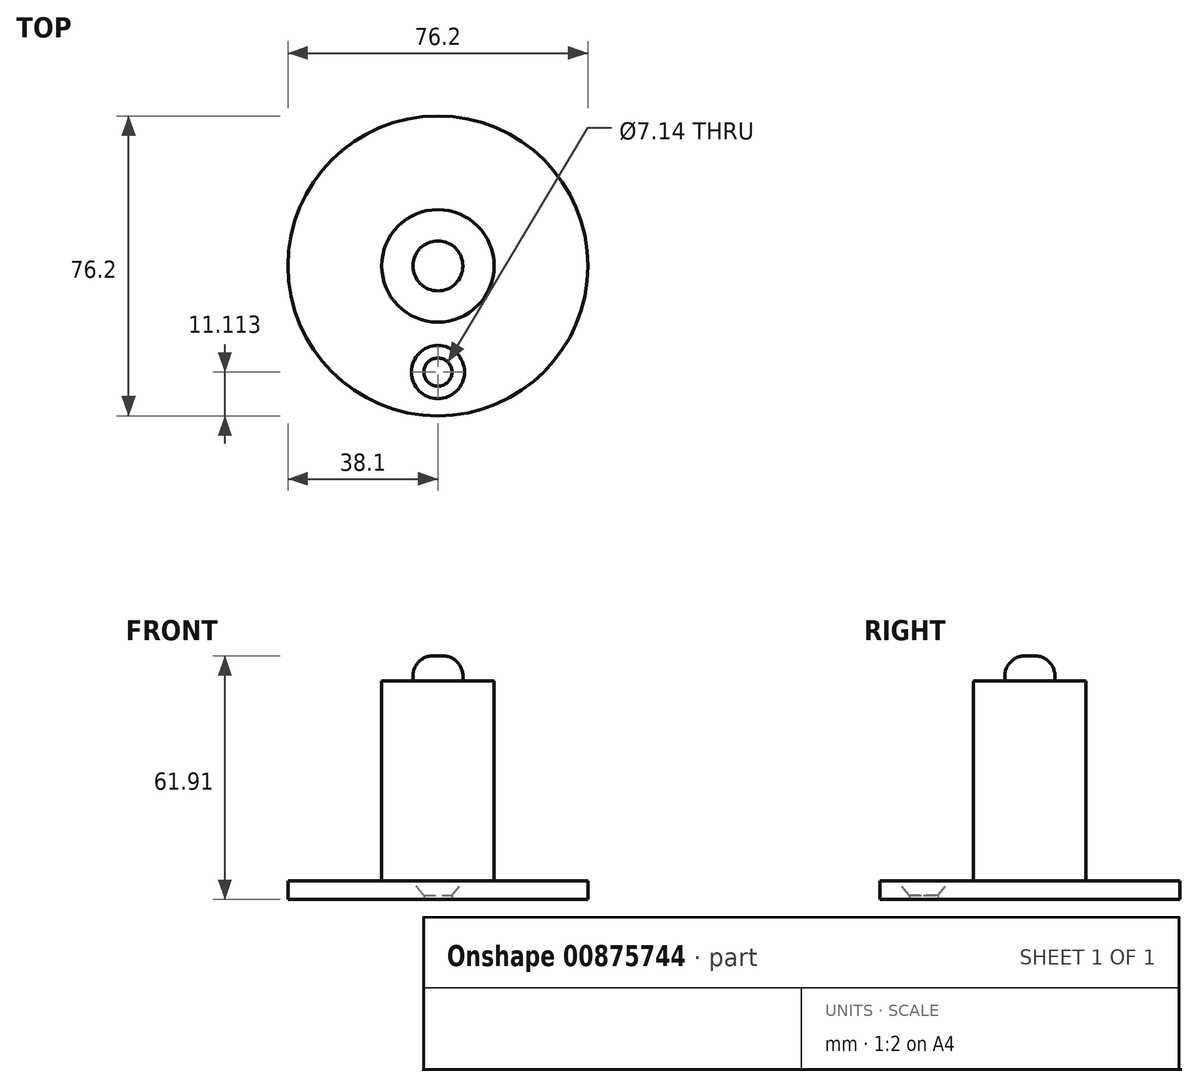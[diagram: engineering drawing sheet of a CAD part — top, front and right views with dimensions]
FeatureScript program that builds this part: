
annotation { "Feature Type Name" : "Feature", "Feature Type Description" : "" }
export const myFeature = defineFeature(function(context is Context, id is Id, definition is map)
    precondition{}
    {
        {
            var Q0;
            Q0=qCreatedBy(makeId("Top.planeOp"),FACE);
            var sketch = newSketch(context, id + "F0", { "sketchPlane" : qUnion([Q0])});
            skCircle(sketch, "E0", {"center": v(0, 0) * mm, "radius": 38.1 * mm});
            skSolve(sketch);
        }
        {
            var Q0;
            Q0=makeQuery(id+"F0.imprint","IMPRINT",FACE,{"disambiguationData":[TD([[makeQuery(id+"F0.imprint","IMPRINT",EDGE,{"derivedFrom":sQuery(id+"F0.wireOp",EDGE,"E0")}),1.0]])]});
            extrude(context, id + "F1", {"entities" : qUnion([Q0]), "depth" : 4.76 * mm, "offsetDistance" : 25.4 * mm});
        }
        {
            var Q0;
            Q0=makeQuery(id+"F1.opExtrude","CAP_FACE",FACE,{"disambiguationData":[OSD([sQuery(id+"F0.wireOp",EDGE,"E0")])],"isStart":false});
            var sketch = newSketch(context, id + "F2", { "sketchPlane" : qUnion([Q0])});
            skCircle(sketch, "E1", {"center": v(0, 0) * mm, "radius": 14.29 * mm});
            skSolve(sketch);
        }
        {
            var Q0;
            Q0=makeQuery(id+"F2.imprint","IMPRINT",FACE,{"disambiguationData":[TD([[makeQuery(id+"F2.imprint","IMPRINT",EDGE,{"derivedFrom":sQuery(id+"F2.wireOp",EDGE,"E1")}),1.0]])]});
            extrude(context, id + "F3", {"entities" : qUnion([Q0]), "operationType" : NewBodyOperationType.ADD, "depth" : 50.8 * mm, "offsetDistance" : 25.4 * mm});
        }
        {
            var Q0;
            Q0=makeQuery(id+"F3.opExtrude","CAP_FACE",FACE,{"disambiguationData":[OSD([sQuery(id+"F2.wireOp",EDGE,"E1")])],"isStart":false});
            var sketch = newSketch(context, id + "F4", { "sketchPlane" : qUnion([Q0])});
            skCircle(sketch, "E2", {"center": v(0, 0) * mm, "radius": 6.35 * mm});
            skSolve(sketch);
        }
        {
            var Q0;
            Q0=makeQuery(id+"F4.imprint","IMPRINT",FACE,{"disambiguationData":[TD([[makeQuery(id+"F4.imprint","IMPRINT",EDGE,{"derivedFrom":sQuery(id+"F4.wireOp",EDGE,"E2")}),1.0]])]});
            extrude(context, id + "F5", {"entities" : qUnion([Q0]), "operationType" : NewBodyOperationType.ADD, "depth" : 6.35 * mm, "offsetDistance" : 25.4 * mm});
        }
        {
            var Q0;
            Q0=makeQuery(id+"F5.opExtrude","CAP_EDGE",EDGE,{"disambiguationData":[OSD([sQuery(id+"F4.wireOp",EDGE,"E2")])],"isStart":false});
            fillet(context, id + "F6", {"entities" : qUnion([Q0]), "radius" : 5.08 * mm, "tangentPropagation" : true, "allowEdgeOverflow" : false});
        }
        {
            var Q0;
            Q0=makeQuery(id+"F1.opExtrude","CAP_FACE",FACE,{"disambiguationData":[OSD([sQuery(id+"F0.wireOp",EDGE,"E0")])],"isStart":false});
            var sketch = newSketch(context, id + "F7", { "sketchPlane" : qUnion([Q0])});
            skPoint(sketch, "E3", {"position": v(0, -26.99) * mm});
            skSolve(sketch);
        }
        {
            var Q0;
            Q0=sQuery(id+"F7.wireOp",VERTEX,"E3");
            var Q1;
            Q1=makeQuery(id+"F1.opExtrude","SWEPT_BODY",BODY,{"disambiguationData":[OSD([sQuery(id+"F0.wireOp",EDGE,"E0")])]});
            hole(context, id + "F8", {"style" : HoleStyle.C_SINK, "endStyle" : HoleEndStyle.BLIND, "standardTappedOrClearance" : lookupTablePath({ "fit" : "Normal (ASME)", "standard" : "ANSI", "size" : "1/4", "type" : "Clearance" }), "standardBlindInLast" : lookupTablePath({ "fit" : "Normal", "standard" : "ANSI", "engagement" : "75%", "pitch" : "20 tpi", "size" : "1/4", "type" : "Clearance & tapped" }), "holeDiameter" : 7.14 * mm, "cSinkDiameter" : 13.5 * mm, "cSinkAngle" : 82 * degree, "majorDiameter" : 6.35 * mm, "holeDepth" : 15.88 * mm, "isTappedThrough" : true, "tappedDepth" : 12.7 * mm, "tapClearance" : 3, "locations" : qUnion([Q0]), "scope" : qUnion([Q1])});
        }
    });
